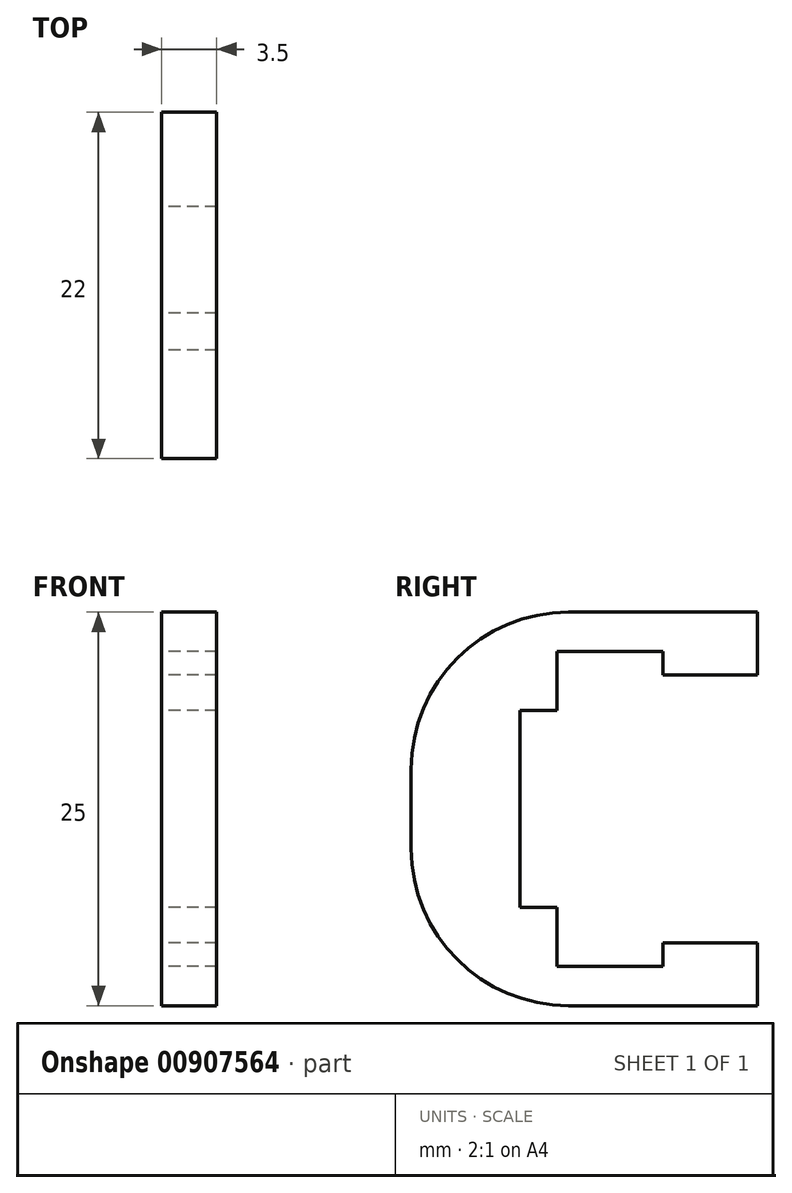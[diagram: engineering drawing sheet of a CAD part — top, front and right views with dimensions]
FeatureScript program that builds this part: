
annotation { "Feature Type Name" : "Feature", "Feature Type Description" : "" }
export const myFeature = defineFeature(function(context is Context, id is Id, definition is map)
    precondition{}
    {
        {
            var Q0;
            Q0=qCreatedBy(makeId("Front.planeOp"),FACE);
            var sketch = newSketch(context, id + "F0", { "sketchPlane" : qUnion([Q0])});
            skLineSegment(sketch, "E0.bottom", {"start": v(-1.75, 12.5) * mm, "end": v(1.75, 12.5) * mm});
            skLineSegment(sketch, "E0.top", {"start": v(-1.75, -12.5) * mm, "end": v(1.75, -12.5) * mm});
            skLineSegment(sketch, "E0.left", {"start": v(-1.75, 12.5) * mm, "end": v(-1.75, -12.5) * mm});
            skLineSegment(sketch, "E0.right", {"start": v(1.75, 12.5) * mm, "end": v(1.75, -12.5) * mm});
            skPoint(sketch, "E0.middle", {"position": v(0, 0) * mm});
            skSolve(sketch);
        }
        {
            var Q0;
            Q0=makeQuery(id+"F0.imprint","IMPRINT",FACE,{"disambiguationData":[TD([[makeQuery(id+"F0.imprint","IMPRINT",EDGE,{"derivedFrom":sQuery(id+"F0.wireOp",EDGE,"E0.bottom")}),-1.0]])]});
            extrude(context, id + "F1", {"entities" : qUnion([Q0]), "depth" : 22 * mm, "offsetDistance" : 25 * mm});
        }
        {
            var Q0;
            Q0=makeQuery(id+"F1.opExtrude","SWEPT_FACE",FACE,{"disambiguationData":[OSD([sQuery(id+"F0.wireOp",EDGE,"E0.left")])]});
            var sketch = newSketch(context, id + "F2", { "sketchPlane" : qUnion([Q0])});
            skLineSegment(sketch, "E1", {"start": v(0, -12.5) * mm, "end": v(0, -8.5) * mm});
            skLineSegment(sketch, "E2", {"start": v(0, -8.5) * mm, "end": v(6, -8.5) * mm});
            skLineSegment(sketch, "E3", {"start": v(6, -8.5) * mm, "end": v(6, -10) * mm});
            skLineSegment(sketch, "E4", {"start": v(6, -10) * mm, "end": v(12.75, -10) * mm});
            skLineSegment(sketch, "E5", {"start": v(12.75, -10) * mm, "end": v(12.75, -6.25) * mm});
            skLineSegment(sketch, "E6", {"start": v(0, 12.5) * mm, "end": v(0, 8.5) * mm});
            skLineSegment(sketch, "E7", {"start": v(0, 8.5) * mm, "end": v(6, 8.5) * mm});
            skLineSegment(sketch, "E8", {"start": v(6, 8.5) * mm, "end": v(6, 10) * mm});
            skLineSegment(sketch, "E9", {"start": v(6, 10) * mm, "end": v(12.75, 10) * mm});
            skLineSegment(sketch, "E10", {"start": v(12.75, 10) * mm, "end": v(12.75, 6.25) * mm});
            skLineSegment(sketch, "E11", {"start": v(12.75, 6.25) * mm, "end": v(15.1, 6.25) * mm});
            skLineSegment(sketch, "E12", {"start": v(15.1, 6.25) * mm, "end": v(15.1, -6.25) * mm});
            skLineSegment(sketch, "E13", {"start": v(15.1, -6.25) * mm, "end": v(12.75, -6.25) * mm});
            skPoint(sketch, "E14.orphan", {"position": v(12.75, 0) * mm});
            skSolve(sketch);
        }
        {
            var Q0;
            {var subQ1=sQuery(id+"F2.wireOp",EDGE,"E2");Q0=makeQuery(id+"F2.imprint","IMPRINT",FACE,{"disambiguationData":[TD([[makeQuery(id+"F2.imprint","IMPRINT",EDGE,{"derivedFrom":subQ1}),1.0]])]});}
            extrude(context, id + "F3", {"entities" : qUnion([Q0]), "operationType" : NewBodyOperationType.REMOVE, "oppositeDirection" : true, "depth" : 25 * mm, "offsetDistance" : 25 * mm});
        }
        {
            var Q0;
            Q0=makeQuery(id+"F1.opExtrude","CAP_EDGE",EDGE,{"disambiguationData":[OSD([sQuery(id+"F0.wireOp",EDGE,"E0.bottom")])],"isStart":false});
            var Q1;
            Q1=makeQuery(id+"F1.opExtrude","CAP_EDGE",EDGE,{"disambiguationData":[OSD([sQuery(id+"F0.wireOp",EDGE,"E0.top")])],"isStart":false});
            fillet(context, id + "F4", {"entities" : qUnion([Q0, Q1]), "radius" : 10 * mm, "tangentPropagation" : true, "allowEdgeOverflow" : false});
        }
    });
